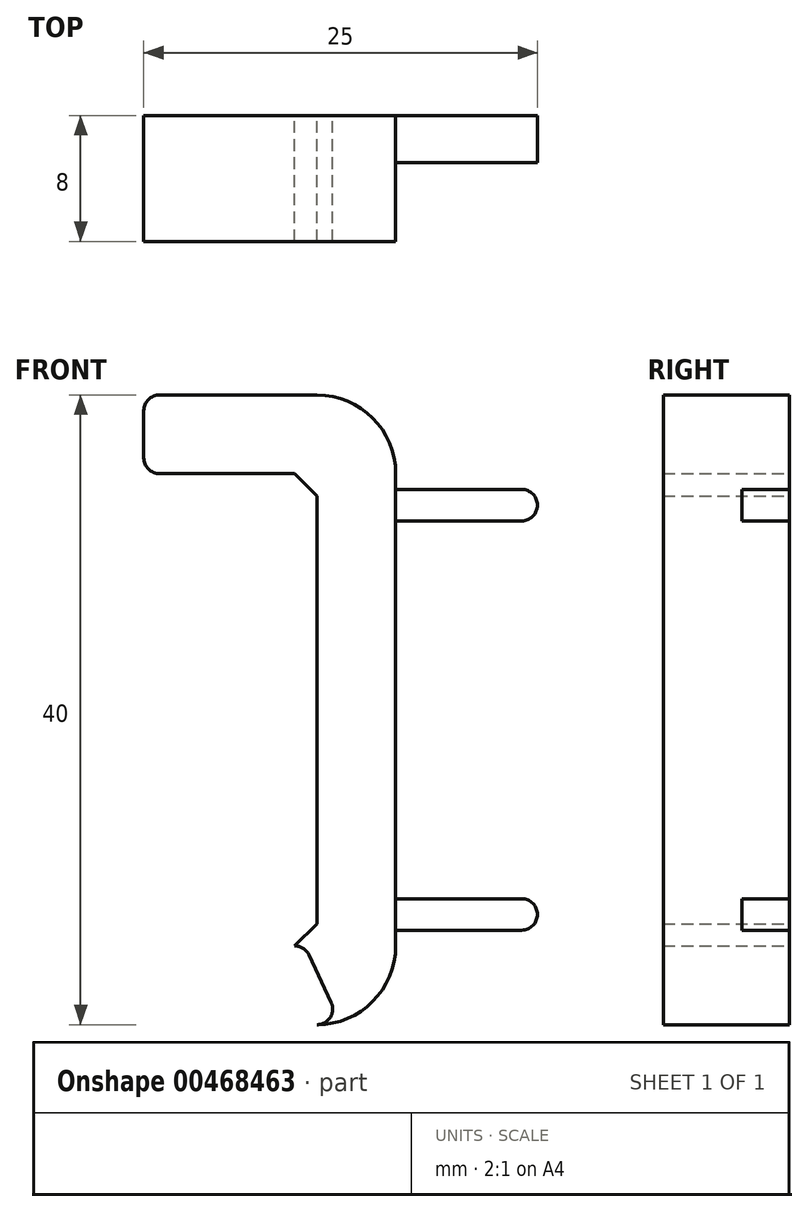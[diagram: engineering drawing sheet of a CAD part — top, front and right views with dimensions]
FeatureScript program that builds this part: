
annotation { "Feature Type Name" : "Feature", "Feature Type Description" : "" }
export const myFeature = defineFeature(function(context is Context, id is Id, definition is map)
    precondition{}
    {
        {
            var Q0;
            Q0=qCreatedBy(makeId("Front.planeOp"),FACE);
            var sketch = newSketch(context, id + "F0", { "sketchPlane" : qUnion([Q0])});
            skLineSegment(sketch, "E0", {"start": v(-15, 15) * mm, "end": v(-6.41, 15) * mm});
            skLineSegment(sketch, "E1", {"start": v(-6.41, 15) * mm, "end": v(-5, 13.59) * mm});
            skLineSegment(sketch, "E2", {"start": v(-5, 13.59) * mm, "end": v(-5, 0) * mm});
            skArc(sketch, "E3", {"start": v(-15, 15) * mm, "mid": v(-15.7, 15.3) * mm, "end": v(-16, 16) * mm});
            skLineSegment(sketch, "E4", {"start": v(-16, 16) * mm, "end": v(-16, 19) * mm});
            skArc(sketch, "E5", {"start": v(-16, 19) * mm, "mid": v(-15.7, 19.7) * mm, "end": v(-15, 20) * mm});
            skLineSegment(sketch, "E6", {"start": v(-15, 20) * mm, "end": v(-5, 20) * mm});
            skArc(sketch, "E7", {"start": v(-5, 20) * mm, "mid": v(-1.46, 18.54) * mm, "end": v(0, 15) * mm});
            skLineSegment(sketch, "E8", {"start": v(0, 15) * mm, "end": v(0, 0) * mm});
            skLineSegment(sketch, "E9", {"start": v(0, 14) * mm, "end": v(8, 14) * mm});
            skLineSegment(sketch, "E10", {"start": v(0, 12) * mm, "end": v(8, 12) * mm});
            skLineSegment(sketch, "E11", {"start": v(-5.7, 14.3) * mm, "end": v(-5, 15) * mm});
            skArc(sketch, "E12", {"start": v(-6.41, 15) * mm, "mid": v(-5.88, 15.16) * mm, "end": v(-5.5, 15.57) * mm});
            skArc(sketch, "E13", {"start": v(-5, 20) * mm, "mid": v(-4.16, 19.54) * mm, "end": v(-4.1, 18.57) * mm});
            skLineSegment(sketch, "E14", {"start": v(-5.5, 15.57) * mm, "end": v(-4.1, 18.57) * mm});
            skArc(sketch, "E15.MirrorCS", {"start": v(-6.41, -15) * mm, "mid": v(-5.88, -15.16) * mm, "end": v(-5.5, -15.57) * mm});
            skLineSegment(sketch, "E16.MirrorCS", {"start": v(-5.7, -14.3) * mm, "end": v(-5, -15) * mm});
            skArc(sketch, "E17.MirrorCS", {"start": v(-15, -15) * mm, "mid": v(-15.7, -15.3) * mm, "end": v(-16, -16) * mm});
            skLineSegment(sketch, "E18.MirrorCS", {"start": v(-6.41, -15) * mm, "end": v(-5, -13.59) * mm});
            skArc(sketch, "E19.MirrorCS", {"start": v(-16, -19) * mm, "mid": v(-15.7, -19.7) * mm, "end": v(-15, -20) * mm});
            skArc(sketch, "E20.MirrorCS", {"start": v(-5, -20) * mm, "mid": v(-1.46, -18.54) * mm, "end": v(0, -15) * mm});
            skLineSegment(sketch, "E21.MirrorCS", {"start": v(-15, -20) * mm, "end": v(-5, -20) * mm});
            skLineSegment(sketch, "E22.MirrorCS", {"start": v(0, -15) * mm, "end": v(0, 0) * mm});
            skLineSegment(sketch, "E23.MirrorCS", {"start": v(-5, -13.59) * mm, "end": v(-5, 0) * mm});
            skArc(sketch, "E24.MirrorCS", {"start": v(-5, -20) * mm, "mid": v(-4.16, -19.54) * mm, "end": v(-4.1, -18.57) * mm});
            skLineSegment(sketch, "E25.MirrorCS", {"start": v(0, -14) * mm, "end": v(8, -14) * mm});
            skLineSegment(sketch, "E26.MirrorCS", {"start": v(-15, -15) * mm, "end": v(-6.41, -15) * mm});
            skLineSegment(sketch, "E27.MirrorCS", {"start": v(-5.5, -15.57) * mm, "end": v(-4.1, -18.57) * mm});
            skLineSegment(sketch, "E28.MirrorCS", {"start": v(0, -12) * mm, "end": v(8, -12) * mm});
            skLineSegment(sketch, "E29.MirrorCS", {"start": v(-16, -16) * mm, "end": v(-16, -19) * mm});
            skArc(sketch, "E30", {"start": v(8, 12) * mm, "mid": v(9, 13) * mm, "end": v(8, 14) * mm});
            skArc(sketch, "E31.MirrorCS", {"start": v(8, -12) * mm, "mid": v(9, -13) * mm, "end": v(8, -14) * mm});
            skSolve(sketch);
        }
        {
            var Q0;
            {var subQ14=sQuery(id+"F0.wireOp",EDGE,"E0");Q0=makeQuery(id+"F0.imprint","IMPRINT",FACE,{"disambiguationData":[TD([[makeQuery(id+"F0.imprint","IMPRINT",EDGE,{"derivedFrom":subQ14}),1.0]])]});}
            var Q1;
            {var subQ14=sQuery(id+"F0.wireOp",EDGE,"E2");Q1=makeQuery(id+"F0.imprint","IMPRINT",FACE,{"disambiguationData":[TD([[makeQuery(id+"F0.imprint","IMPRINT",EDGE,{"derivedFrom":subQ14}),1.0]])]});}
            var Q2;
            Q2=makeQuery(id+"F0.imprint","IMPRINT",FACE,{"disambiguationData":[TD([[makeQuery(id+"F0.imprint","IMPRINT",EDGE,{"derivedFrom":sQuery(id+"F0.wireOp",EDGE,"E15.MirrorCS")}),-1.0]])]});
            var Q3;
            {var subQ2=sQuery(id+"F0.wireOp",EDGE,"E9");Q3=makeQuery(id+"F0.imprint","IMPRINT",FACE,{"disambiguationData":[TD([[makeQuery(id+"F0.imprint","IMPRINT",EDGE,{"derivedFrom":subQ2}),-1.0]])]});}
            var Q4;
            {var subQ0=sQuery(id+"F0.wireOp",EDGE,"E25.MirrorCS");Q4=makeQuery(id+"F0.imprint","IMPRINT",FACE,{"disambiguationData":[TD([[makeQuery(id+"F0.imprint","IMPRINT",EDGE,{"derivedFrom":subQ0}),1.0]])]});}
            extrude(context, id + "F1", {"entities" : qUnion([Q0, Q1, Q2, Q3, Q4]), "depth" : 3 * mm});
        }
        {
            var Q0;
            Q0=makeQuery(id+"F0.imprint","IMPRINT",FACE,{"disambiguationData":[TD([[makeQuery(id+"F0.imprint","IMPRINT",EDGE,{"derivedFrom":sQuery(id+"F0.wireOp",EDGE,"E0")}),1.0]])]});
            var Q1;
            Q1=makeQuery(id+"F0.imprint","IMPRINT",FACE,{"disambiguationData":[TD([[makeQuery(id+"F0.imprint","IMPRINT",EDGE,{"derivedFrom":sQuery(id+"F0.wireOp",EDGE,"E15.MirrorCS")}),-1.0]])]});
            var Q2;
            {var subQ10=sQuery(id+"F0.wireOp",EDGE,"E2");Q2=makeQuery(id+"F0.imprint","IMPRINT",FACE,{"disambiguationData":[TD([[makeQuery(id+"F0.imprint","IMPRINT",EDGE,{"derivedFrom":subQ10}),1.0]])]});}
            extrude(context, id + "F2", {"entities" : qUnion([Q0, Q1, Q2]), "operationType" : NewBodyOperationType.ADD, "depth" : 5 * mm});
        }
        {
            var Q0;
            Q0=makeQuery(id+"F0.imprint","IMPRINT",FACE,{"disambiguationData":[TD([[makeQuery(id+"F0.imprint","IMPRINT",EDGE,{"derivedFrom":sQuery(id+"F0.wireOp",EDGE,"E0")}),1.0]])]});
            var Q1;
            Q1=makeQuery(id+"F0.imprint","IMPRINT",FACE,{"disambiguationData":[TD([[makeQuery(id+"F0.imprint","IMPRINT",EDGE,{"derivedFrom":sQuery(id+"F0.wireOp",EDGE,"E15.MirrorCS")}),-1.0]])]});
            extrude(context, id + "F3", {"entities" : qUnion([Q0, Q1]), "operationType" : NewBodyOperationType.ADD, "depth" : 8 * mm});
        }
    });
